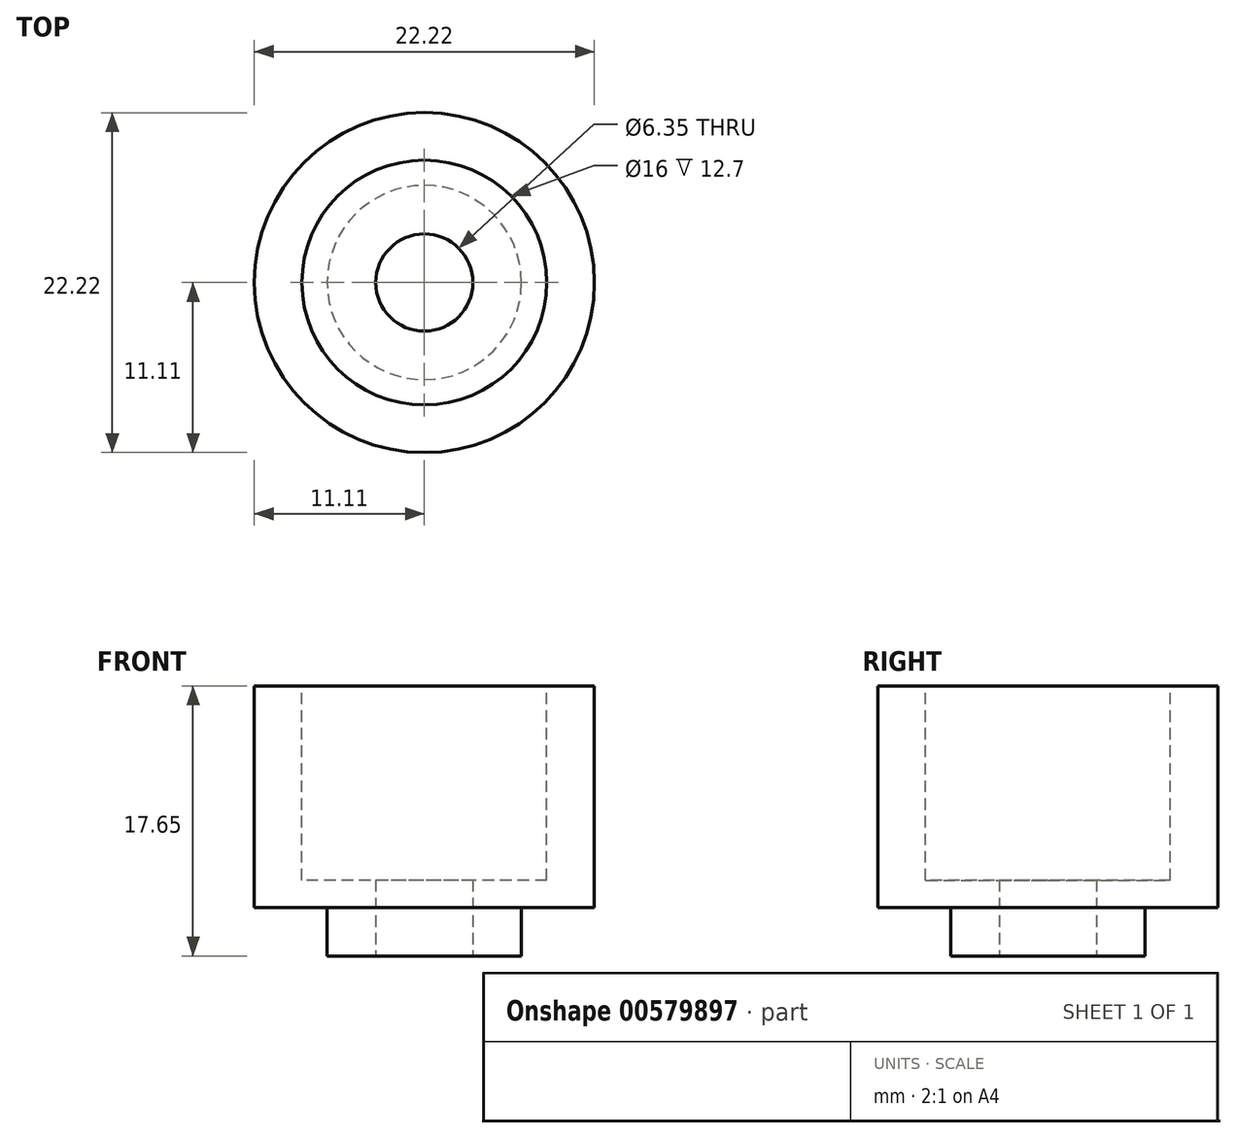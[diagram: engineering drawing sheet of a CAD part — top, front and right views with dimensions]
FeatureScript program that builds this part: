
annotation { "Feature Type Name" : "Feature", "Feature Type Description" : "" }
export const myFeature = defineFeature(function(context is Context, id is Id, definition is map)
    precondition{}
    {
        {
            var Q0;
            Q0=qCreatedBy(makeId("Top.planeOp"),FACE);
            var sketch = newSketch(context, id + "F0", { "sketchPlane" : qUnion([Q0])});
            skCircle(sketch, "E0", {"center": v(0, 0) * mm, "radius": 6.35 * mm});
            skCircle(sketch, "E1", {"center": v(0, 0) * mm, "radius": 3.18 * mm});
            skSolve(sketch);
        }
        {
            var Q0;
            Q0 = qSketchRegion(id + "F0", true);
            extrude(context, id + "F1", {"entities" : qUnion([Q0]), "depth" : 3.17 * mm, "offsetDistance" : 25.4 * mm});
        }
        {
            var Q0;
            Q0=makeQuery(id+"F1.opExtrude","CAP_FACE",FACE,{"disambiguationData":[OSD([sQuery(id+"F0.wireOp",EDGE,"E0"),sQuery(id+"F0.wireOp",EDGE,"E1")])],"isStart":false});
            var sketch = newSketch(context, id + "F2", { "sketchPlane" : qUnion([Q0])});
            skCircle(sketch, "E2", {"center": v(0, 0) * mm, "radius": 3.18 * mm});
            skCircle(sketch, "E3", {"center": v(0, 0) * mm, "radius": 11.11 * mm});
            skSolve(sketch);
        }
        {
            var Q0;
            Q0 = qSketchRegion(id + "F2", true);
            extrude(context, id + "F3", {"entities" : qUnion([Q0]), "operationType" : NewBodyOperationType.ADD, "depth" : 14.48 * mm, "offsetDistance" : 25.4 * mm});
        }
        {
            var Q0;
            Q0=makeQuery(id+"F3.opExtrude","CAP_FACE",FACE,{"disambiguationData":[OSD([sQuery(id+"F2.wireOp",EDGE,"E2"),sQuery(id+"F2.wireOp",EDGE,"E3")])],"isStart":false});
            var sketch = newSketch(context, id + "F4", { "sketchPlane" : qUnion([Q0])});
            skCircle(sketch, "E4", {"center": v(0, 0) * mm, "radius": 8 * mm});
            skSolve(sketch);
        }
        {
            var Q0;
            Q0 = qSketchRegion(id + "F4", true);
            extrude(context, id + "F5", {"entities" : qUnion([Q0]), "operationType" : NewBodyOperationType.REMOVE, "oppositeDirection" : true, "depth" : 12.7 * mm, "offsetDistance" : 25.4 * mm});
        }
    });
